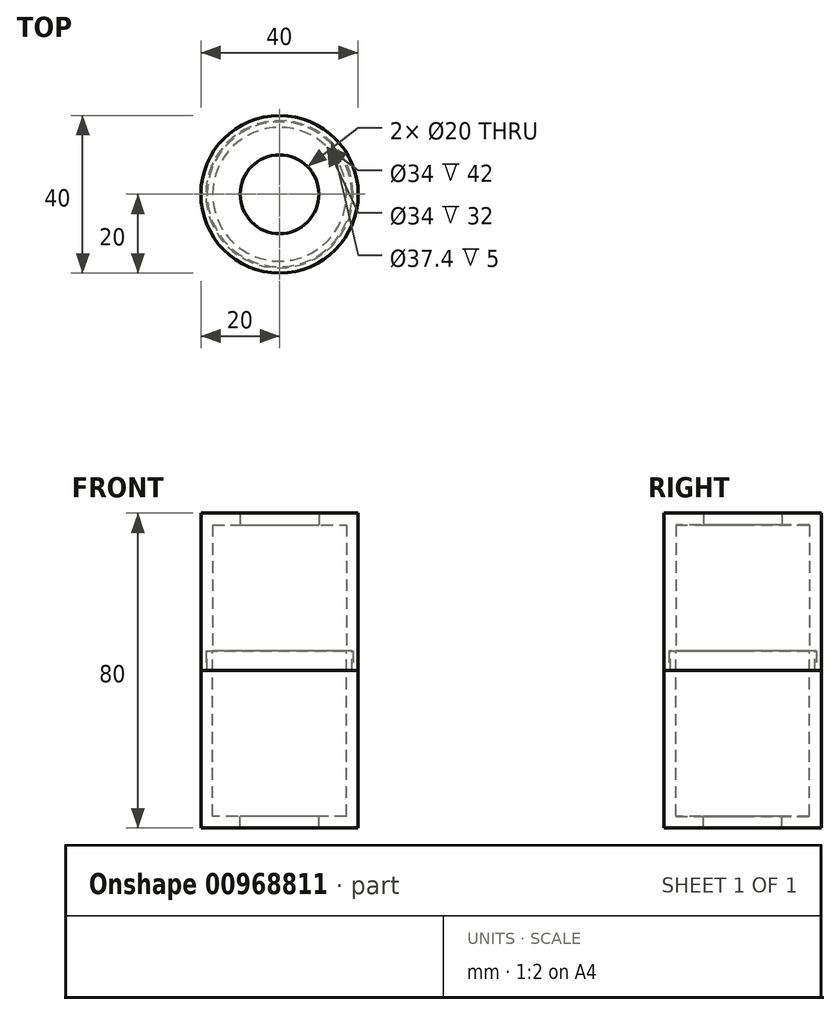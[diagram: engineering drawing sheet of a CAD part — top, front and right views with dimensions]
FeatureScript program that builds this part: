
annotation { "Feature Type Name" : "Feature", "Feature Type Description" : "" }
export const myFeature = defineFeature(function(context is Context, id is Id, definition is map)
    precondition{}
    {
        {
            var Q0;
            Q0=qCreatedBy(makeId("Front.planeOp"),FACE);
            var sketch = newSketch(context, id + "F0", { "sketchPlane" : qUnion([Q0])});
            skLineSegment(sketch, "E0", {"start": v(0, 0) * mm, "end": v(0, 39.81) * mm, "construction": true});
            skLineSegment(sketch, "E1", {"start": v(10, 40) * mm, "end": v(20, 40) * mm});
            skLineSegment(sketch, "E2", {"start": v(20, 40) * mm, "end": v(20, 0) * mm});
            skLineSegment(sketch, "E3.0", {"start": v(17, 37) * mm, "end": v(17, 5) * mm});
            skLineSegment(sketch, "E3.1", {"start": v(10, 37) * mm, "end": v(17, 37) * mm});
            skLineSegment(sketch, "E4", {"start": v(10, 37) * mm, "end": v(10, 40) * mm});
            skLineSegment(sketch, "E5", {"start": v(20, 0) * mm, "end": v(18.7, 0) * mm});
            skLineSegment(sketch, "E6", {"start": v(18.7, 0) * mm, "end": v(18.7, 5) * mm});
            skLineSegment(sketch, "E7", {"start": v(18.7, 5) * mm, "end": v(17, 5) * mm});
            skSolve(sketch);
        }
        {
            var Q0;
            Q0=makeQuery(id+"F0.imprint","IMPRINT",FACE,{"disambiguationData":[TD([[makeQuery(id+"F0.imprint","IMPRINT",EDGE,{"derivedFrom":sQuery(id+"F0.wireOp",EDGE,"E1")}),-1.0]])]});
            var Q1;
            Q1=sQuery(id+"F0.wireOp",EDGE,"E0");
            revolve(context, id + "F1", {"surfaceOperationType" : NewSurfaceOperationType.NEW, "entities" : qUnion([Q0]), "axis" : qUnion([Q1]), "revolveType" : RevolveType.FULL});
        }
        {
            var Q0;
            Q0=qCreatedBy(makeId("Front.planeOp"),FACE);
            var sketch = newSketch(context, id + "F2", { "sketchPlane" : qUnion([Q0])});
            skLineSegment(sketch, "E8", {"start": v(0, 0) * mm, "end": v(0, -22.7) * mm, "construction": true});
            skLineSegment(sketch, "E9", {"start": v(20, 0) * mm, "end": v(20, -40) * mm});
            skLineSegment(sketch, "E10", {"start": v(20, -40) * mm, "end": v(10, -40) * mm});
            skLineSegment(sketch, "E11.0", {"start": v(17, -37) * mm, "end": v(10, -37) * mm});
            skLineSegment(sketch, "E11.1", {"start": v(17, 0) * mm, "end": v(17, -37) * mm});
            skLineSegment(sketch, "E12", {"start": v(10, -37) * mm, "end": v(10, -40) * mm});
            skPoint(sketch, "E12.endSnap0", {"position": v(10, -40) * mm});
            skLineSegment(sketch, "E13", {"start": v(17, 0) * mm, "end": v(17, 5) * mm});
            skLineSegment(sketch, "E14", {"start": v(17, 5) * mm, "end": v(18.4, 5) * mm});
            skLineSegment(sketch, "E15", {"start": v(18.4, 5) * mm, "end": v(18.4, 0) * mm});
            skLineSegment(sketch, "E16", {"start": v(18.4, 0) * mm, "end": v(20, 0) * mm});
            skSolve(sketch);
        }
        {
            var Q0;
            Q0=makeQuery(id+"F2.imprint","IMPRINT",FACE,{"disambiguationData":[TD([[makeQuery(id+"F2.imprint","IMPRINT",EDGE,{"derivedFrom":sQuery(id+"F2.wireOp",EDGE,"E9")}),-1.0]])]});
            var Q1;
            Q1=sQuery(id+"F2.wireOp",EDGE,"E8");
            revolve(context, id + "F3", {"surfaceOperationType" : NewSurfaceOperationType.NEW, "entities" : qUnion([Q0]), "axis" : qUnion([Q1]), "revolveType" : RevolveType.FULL});
        }
    });
